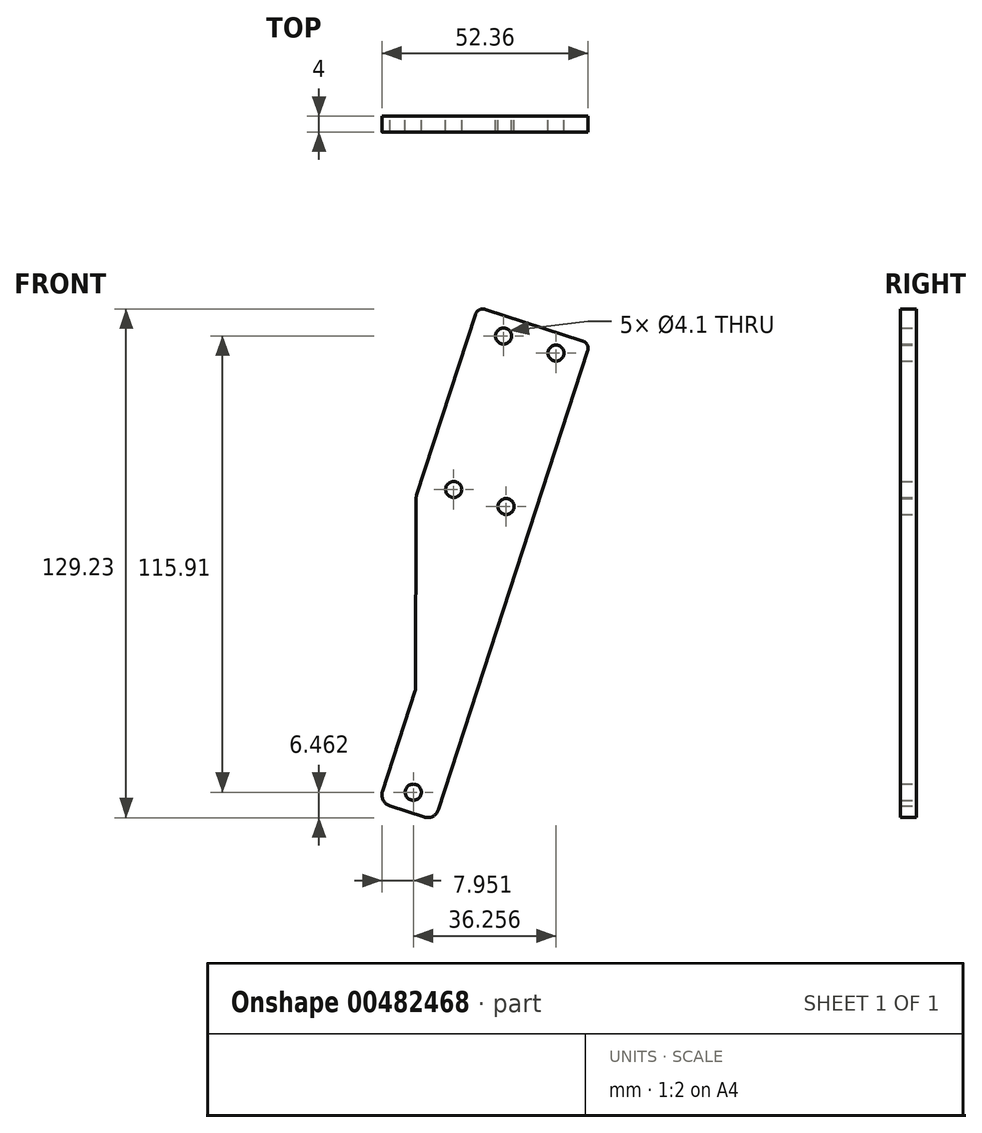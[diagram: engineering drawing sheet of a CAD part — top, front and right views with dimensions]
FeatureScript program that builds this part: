
annotation { "Feature Type Name" : "Feature", "Feature Type Description" : "" }
export const myFeature = defineFeature(function(context is Context, id is Id, definition is map)
    precondition{}
    {
        {
            var Q0;
            Q0=qCreatedBy(makeId("Front.planeOp"),FACE);
            var sketch = newSketch(context, id + "F0", { "sketchPlane" : qUnion([Q0])});
            skLineSegment(sketch, "E0", {"start": v(-38.12, -24.18) * mm, "end": v(-16.15, 43.44) * mm});
            skLineSegment(sketch, "E1", {"start": v(-54.37, -25.67) * mm, "end": v(-62.67, -51.2) * mm});
            skLineSegment(sketch, "E2", {"start": v(-48.4, -55.85) * mm, "end": v(-38.12, -24.18) * mm});
            skLineSegment(sketch, "E3", {"start": v(-54.87, -51.47) * mm, "end": v(-12.93, 77.6) * mm, "construction": true});
            skArc(sketch, "E4.filletArc", {"start": v(-52.19, -57.78) * mm, "mid": v(-49.9, -57.6) * mm, "end": v(-48.4, -55.85) * mm});
            skArc(sketch, "E5.filletArc", {"start": v(-62.67, -51.2) * mm, "mid": v(-62.5, -53.47) * mm, "end": v(-60.8, -54.97) * mm});
            skLineSegment(sketch, "E6", {"start": v(-14.77, 10.5) * mm, "end": v(-63.8, 26.43) * mm, "construction": true});
            skLineSegment(sketch, "E7", {"start": v(-16.15, 43.44) * mm, "end": v(-9.94, 62.55) * mm});
            skLineSegment(sketch, "E8", {"start": v(-25.7, 14.05) * mm, "end": v(-10.55, 60.65) * mm});
            skLineSegment(sketch, "E9", {"start": v(-11.84, 63.17) * mm, "end": v(-24.2, 67.19) * mm});
            skPoint(sketch, "E10.orphan", {"position": v(0, 93.13) * mm});
            skCircle(sketch, "E11", {"center": v(-54.87, -51.47) * mm, "radius": 2.05 * mm});
            skCircle(sketch, "E12", {"center": v(-18.61, 60.12) * mm, "radius": 2.05 * mm});
            skCircle(sketch, "E13", {"center": v(-31.28, 21.12) * mm, "radius": 2.05 * mm});
            skLineSegment(sketch, "E14", {"start": v(-24.2, 67.19) * mm, "end": v(-36.56, 71.2) * mm});
            skLineSegment(sketch, "E15", {"start": v(-39.09, 69.92) * mm, "end": v(-53.98, 24.07) * mm});
            skLineSegment(sketch, "E16", {"start": v(-54.87, -51.47) * mm, "end": v(-79.15, -43.58) * mm, "construction": true});
            skPoint(sketch, "E17.end.orphan", {"position": v(-56.18, -31.23) * mm});
            skPoint(sketch, "E18", {"position": v(-54.28, -25.37) * mm});
            skLineSegment(sketch, "E19", {"start": v(-54.23, 22.53) * mm, "end": v(-54.28, -25.06) * mm});
            skLineSegment(sketch, "E20", {"start": v(-18.61, 60.12) * mm, "end": v(-43.33, 68.15) * mm, "construction": true});
            skLineSegment(sketch, "E21", {"start": v(-31.28, 21.12) * mm, "end": v(-57.91, 29.78) * mm, "construction": true});
            skCircle(sketch, "E22", {"center": v(-31.93, 64.44) * mm, "radius": 2.05 * mm});
            skCircle(sketch, "E23", {"center": v(-44.6, 25.45) * mm, "radius": 2.05 * mm});
            skPoint(sketch, "E24.visualSharp", {"position": v(-38.47, 71.82) * mm});
            skArc(sketch, "E24.filletArc", {"start": v(-36.56, 71.2) * mm, "mid": v(-38.1, 71.09) * mm, "end": v(-39.09, 69.92) * mm});
            skPoint(sketch, "E25.visualSharp", {"position": v(-9.94, 62.55) * mm});
            skArc(sketch, "E25.filletArc", {"start": v(-10.55, 60.65) * mm, "mid": v(-10.67, 62.18) * mm, "end": v(-11.84, 63.17) * mm});
            skPoint(sketch, "E26.visualSharp", {"position": v(-54.23, 23.32) * mm});
            skArc(sketch, "E26.filletArc", {"start": v(-53.98, 24.07) * mm, "mid": v(-54.17, 23.31) * mm, "end": v(-54.23, 22.53) * mm});
            skPoint(sketch, "E27.orphan", {"position": v(-30.41, 48.07) * mm});
            skArc(sketch, "E28.filletArc", {"start": v(-54.37, -25.67) * mm, "mid": v(-54.3, -25.37) * mm, "end": v(-54.28, -25.06) * mm});
            skLineSegment(sketch, "E29", {"start": v(-60.8, -54.97) * mm, "end": v(-52.19, -57.78) * mm});
            skSolve(sketch);
        }
        {
            var Q0;
            Q0 = qSketchRegion(id + "F0", true);
            extrude(context, id + "F1", {"entities" : qUnion([Q0]), "depth" : 4 * mm, "offsetDistance" : 25 * mm});
        }
    });
